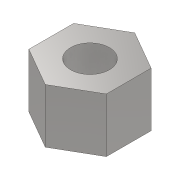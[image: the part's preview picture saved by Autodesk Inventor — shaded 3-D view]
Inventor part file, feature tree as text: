
AUTODESK INVENTOR PART (.ipt)
format: ipt  version: 2022 (Build 260153000, 153)  size: 90,624 bytes
history: native  units: mm
features: extrude x1, sketch x1
ambient origin geometry x8: Origin, YZ Plane, XZ Plane, XY Plane, X Axis, Y Axis, Z Axis, Center Point
bodies: Solid1 (feature_tree)
feature tree (2):
  extrude  "Extrusion1"  Depth=2.8mm
  sketch  "Sketch1"  dims[d0=4.0mm d1=2.0mm d2=2.8mm d3=0.0mm]
